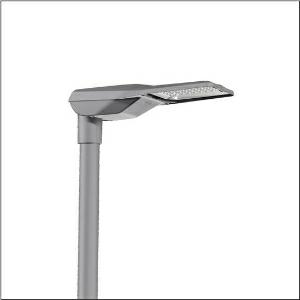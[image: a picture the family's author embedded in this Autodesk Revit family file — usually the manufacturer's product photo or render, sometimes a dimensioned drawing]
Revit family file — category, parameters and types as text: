
# Revit family: streetlight_sl_21_iq_mini___p0_8a_5xe2u31d08hb_de2c
name_source: partatom
category: Lighting Fixtures
units: mm (PartAtom-declared; Revit-internal decimal feet)

## family parameters
Cut with Voids When Loaded = No
Host = Face
Light Source = No
Part Type = Normal
Room Calculation Point = No
Round Connector Dimension = Use Diameter
Shared = No

## types (1)
- --- (1 x LED, 9540 lm, 70.9 W, 3000K)
    Apparent Load = 71 VA
    CIE Flux Codes = 33 69 96 100 100
    Color Rendering = 70
    Color Temperature = 3000K
    Default Elevation = 1800 mm
    Description = Streetlight SL 21 iQ mini, mast luminaire, primary light control with lens, of PMMA, primary optical cover: cover, of toughened safety glass, transparent, light distribution: P0.8a, light emission: direct distribution, primary light characteristic: asymmetric, installation type: post-top, side-entry, LED, High Power LED, rated luminous flux: 9.540lm, luminous efficacy: 135lm/W, light colour: 730, colour temperature: 3000K, control gear: iQ-Comfort, control: pre-setting: linear dimming characteristic, Auto-Match, Temp-Guard, Lumen-Switch, Night-Set, Smart-Wire, Light-Fading, Desk-Remote (wireless, voltage-free reading and setting of iQ features in the workshop via application-optimized NFC function/RFID function), optimised constant luminous flux control (CLO 2.0), mains connection: 220..240V, AC, 50/60Hz, start of lifetime: 71W, end of service life: 75W, reduction: 31W, luminaire housing, of diecast aluminium, powder-coated, SITECO metallic grey (DB 702S), corrosivity category C5 high according to DIN EN ISO 12944, please order mast flange separately, inclination adjustable: 0°, 5°, 10°, 15°, sealing non-destructively replaceable, multi-level sealing system, length: 628mm, width: 235mm, height: 110mm, mast flange for spigot size: 42mm (side-entry): 5XC10008XM4, 60/48mm (side-entry/post-top): 5XC10108XM2, 76/60mm (side-entry/post-top): 5XC10108XM1, mounting height: 4..8m, protection rating (complete): IP66, insulation class (complete): insulation class II (safety insulation), certification: CE, ENEC, ENEC+, VDE, impact resistance: IK10, permissible operating ambient temperature for outdoor applications: -40..+50°C, standard-compliant lighting for roads and squares, packaging unit: 1 piece

Light Distribution: P0.8a
    Height = 110 mm
    Lamp = 1 x LED
    Lamp Light Flux = 9540 lm
    Lamp Power = 70.9 W
    Lamp count = 1
    Length = 625 mm
    Luminous efficacy = 135 lm/W
    Manufacturer = Siteco
    ModVariant = No
    Model = 5XE2U31D08HB
    Number of Poles = 1
    OnlyDefault = Yes
    Power Factor = 1
    Product Name = Streetlight SL 21 iQ mini | P0.8a
    Product group = mast luminaire | pylon top
    ProductGroupID = 6100
    Protection Class = Protection class II
    Protection Degree = IP 66
    RLX_Detail_Level = 1
    RLX_Emergency_Light_Flux = 0 lm
    RLX_Emergency_Type = 0
    RLX_Emergency_Type_DB = No
    RlxData = <blob elided: 92113 chars, md5=2abb323c>
    Socket = socket
    Standby Power = 0 W
    System Light Flux = 9540 lm
    System Power = 71 W
    Type Comments = factory setting: luminous flux: 100 % | dim-lin: 254 | 711 mA
    Type Image = l_1003519.jpg
    URL = http://relux.com
    VarID = @adj_080181
    Voltage = 0 V
    Weight = 0.00 kg
    Width = 234 mm

## geometry (parser evidence)
native form markers: Blend x4, Sweep x10
no freeform markers — native parametric forms only
